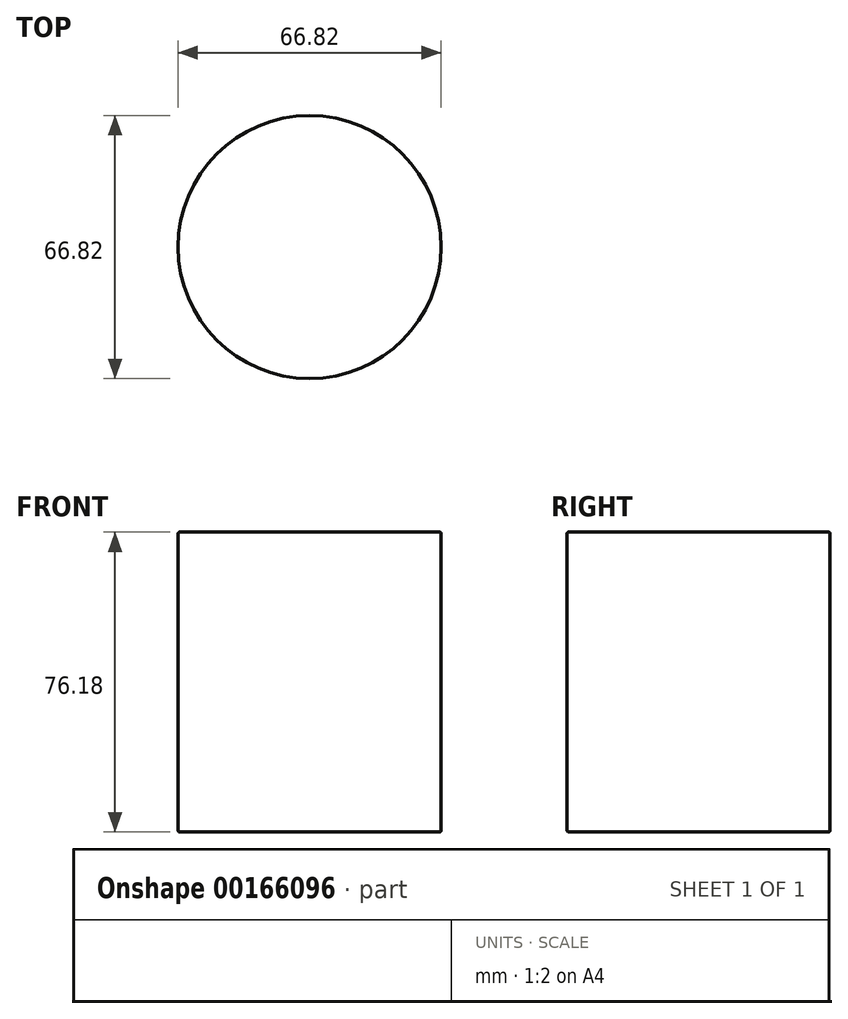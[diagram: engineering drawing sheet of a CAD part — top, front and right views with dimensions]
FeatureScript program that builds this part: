
annotation { "Feature Type Name" : "Feature", "Feature Type Description" : "" }
export const myFeature = defineFeature(function(context is Context, id is Id, definition is map)
    precondition{}
    {
        {
            var Q0;
            Q0=qCreatedBy(makeId("Top.planeOp"),FACE);
            var sketch = newSketch(context, id + "F0", { "sketchPlane" : qUnion([Q0])});
            skCircle(sketch, "E0", {"center": v(0, 0) * mm, "radius": 33.41 * mm});
            skSolve(sketch);
        }
        {
            var Q0;
            Q0=makeQuery(id+"F0.imprint","IMPRINT",FACE,{"disambiguationData":[TD([[makeQuery(id+"F0.imprint","IMPRINT",EDGE,{"derivedFrom":sQuery(id+"F0.wireOp",EDGE,"E0")}),1.0]])]});
            extrude(context, id + "F1", {"entities" : qUnion([Q0]), "depth" : 38.1 * mm});
        }
        {
            var Q0;
            Q0=makeQuery(id+"F1.opExtrude","SWEPT_BODY",BODY,{"disambiguationData":[OSD([sQuery(id+"F0.wireOp",EDGE,"E0")])]});
            var Q1;
            Q1=qCreatedBy(makeId("Top.planeOp"),FACE);
            mirror(context, id + "F2", {"operationType" : NewBodyOperationType.ADD, "entities" : qUnion([Q0]), "mirrorPlane" : qUnion([Q1])});
        }
        {
            var Q0;
            Q0=makeQuery(id+"F2.opPattern","COPY",EDGE,{"derivedFrom":makeQuery(id+"F1.opExtrude","CAP_EDGE",EDGE,{"disambiguationData":[OSD([sQuery(id+"F0.wireOp",EDGE,"E0")])],"isStart":false}),"instanceName":"1"});
            var Q1;
            Q1=makeQuery(id+"F1.opExtrude","CAP_EDGE",EDGE,{"disambiguationData":[OSD([sQuery(id+"F0.wireOp",EDGE,"E0")])],"isStart":false});
            fillet(context, id + "F3", {"entities" : qUnion([Q0, Q1]), "radius" : 0.38 * mm, "allowEdgeOverflow" : false});
        }
    });
